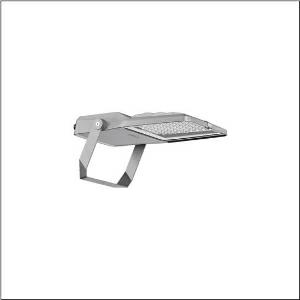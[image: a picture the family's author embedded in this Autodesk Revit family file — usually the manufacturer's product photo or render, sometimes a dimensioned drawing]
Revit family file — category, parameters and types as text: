
# Revit family: floodlight_fl_21_iq_mini___pl64_5xa7771d4e1a_9fb1
name_source: partatom
category: Lighting Fixtures
units: mm (PartAtom-declared; Revit-internal decimal feet)

## family parameters
Cut with Voids When Loaded = No
Host = Face
Light Source = No
Part Type = Normal
Room Calculation Point = No
Round Connector Dimension = Use Diameter
Shared = No

## types (1)
- --- (1 x LED, 17970 lm, 143 W, 4000K)
    Apparent Load = 143 VA
    CIE Flux Codes = 28 80 98 100 100
    Color Rendering = 70
    Color Temperature = 4000K
    Default Elevation = 1800 mm
    Description = Floodlight FL 21 iQ mini, floodlight, primary light control with lens, of PMMA, primary optical cover: protective disc, of toughened safety glass, transparent, light distribution: PL64, light emission: direct distribution, installation type: surface-mounted, LED, High Power LED, rated luminous flux: 17.970lm, luminous efficacy: 126lm/W, light colour: 740, colour temperature: 4000K, control gear: iQ Comfort/DALI, control: Auto-Match, Temp-Guard, Lumen-Switch, Night-Set, Smart-Wire, Light-Fading, Desk-Remote (wireless, voltage-free reading and setting of iQ features in the workshop via application-optimized NFC function/RFID function), optimised constant luminous flux control (CLO 2.0), with terminal, 6-pole, mains connection: 220..240V, AC, 50/60Hz, start of lifetime: 143W, end of service life: 152W, reduction: 61W, luminaire housing, of diecast aluminium, powder-coated, Siteco® metallic grey (DB 702S), corrosivity category C5 mid according to DIN EN ISO 12944, suitable for swimming pools, chlorine-resistant, sealing non-destructively replaceable, mounting bracket, of steel, galvanised, powder-coated, Siteco® metallic grey (DB 702S), protection rating (complete): IP66, insulation class (complete): insulation class II (safety insulation), certification: CE, ENEC, VDE, protection symbol: D, impact resistance: IK08, permissible operating ambient temperature: -40..+40°C, permissible operating ambient temperature for outdoor applications: -40..+50°C, standard: DIN EN 12944, LABS conformity tested according to VDMA 24364:2018-05, packaging unit: 1 piece

Light Distribution: PL64
    Height = 70 mm
    Lamp = 1 x LED
    Lamp Light Flux = 17970 lm
    Lamp Power = 143 W
    Lamp count = 1
    Length = 485 mm
    Luminous efficacy = 126 lm/W
    Manufacturer = Siteco
    ModVariant = No
    Model = 5XA7771D4E1A
    Number of Poles = 1
    OnlyDefault = Yes
    Power Factor = 1
    Product Name = Floodlight FL 21 iQ mini | PL64
    Product group = floodlight | pylon annexe
    ProductGroupID = 6201
    Protection Class = Protection class II
    Protection Degree = IP 66
    RLX_Detail_Level = 1
    RLX_Emergency_Light_Flux = 0 lm
    RLX_Emergency_Type = 0
    RLX_Emergency_Type_DB = No
    RlxData = <blob elided: 96565 chars, md5=ecdf7719>
    Socket = socket
    Standby Power = 0 W
    System Light Flux = 17970 lm
    System Power = 143 W
    Type Comments = factory setting: luminous flux: 100 % | dim-lin: 254 | 730 mA
    Type Image = l_1006845.jpg
    URL = http://relux.com
    VarID = @adj_187495
    Voltage = 0 V
    Weight = 0.00 kg
    Width = 337 mm

## geometry (parser evidence)
native form markers: Blend x4, Sweep x12
no freeform markers — native parametric forms only
